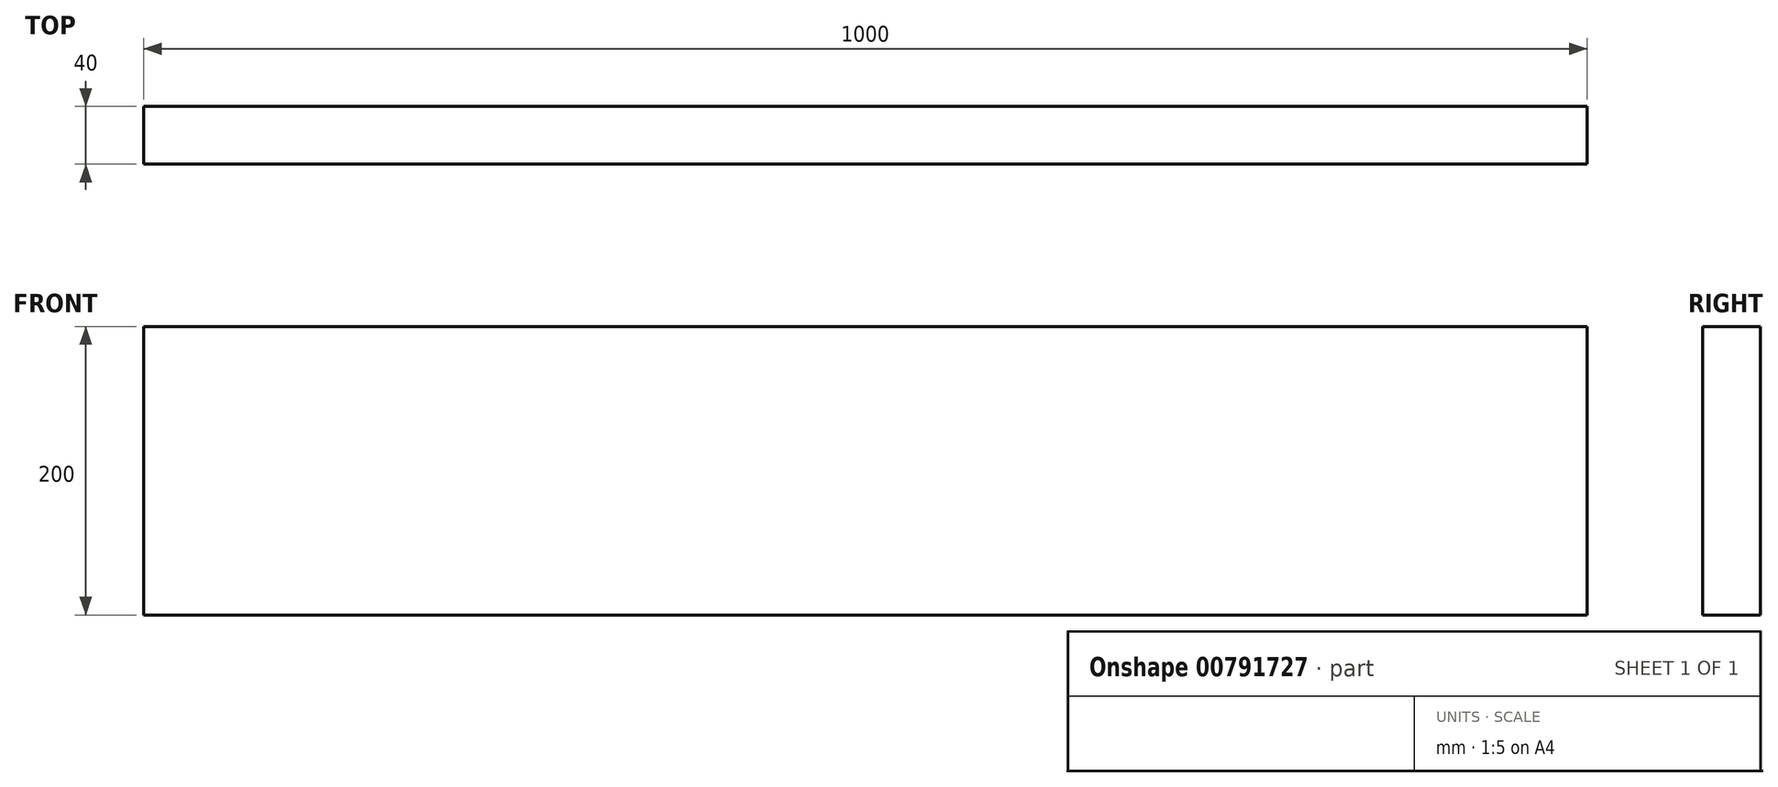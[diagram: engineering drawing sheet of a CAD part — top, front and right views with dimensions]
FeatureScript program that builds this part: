
annotation { "Feature Type Name" : "Feature", "Feature Type Description" : "" }
export const myFeature = defineFeature(function(context is Context, id is Id, definition is map)
    precondition{}
    {
        {
            var Q0;
            Q0=qCreatedBy(makeId("Front.planeOp"),FACE);
            var sketch = newSketch(context, id + "F0", { "sketchPlane" : qUnion([Q0])});
            skLineSegment(sketch, "E0.bottom", {"start": v(-499.55, 99.3) * mm, "end": v(500.45, 99.3) * mm});
            skLineSegment(sketch, "E0.top", {"start": v(-499.55, -100.7) * mm, "end": v(500.45, -100.7) * mm});
            skLineSegment(sketch, "E0.left", {"start": v(-499.55, 99.3) * mm, "end": v(-499.55, -100.7) * mm});
            skLineSegment(sketch, "E0.right", {"start": v(500.45, 99.3) * mm, "end": v(500.45, -100.7) * mm});
            skSolve(sketch);
        }
        {
            var Q0;
            Q0 = qSketchRegion(id + "F0", true);
            extrude(context, id + "F1", {"entities" : qUnion([Q0]), "endBound" : BoundingType.SYMMETRIC, "depth" : 40 * mm, "offsetDistance" : 25 * mm});
        }
    });
